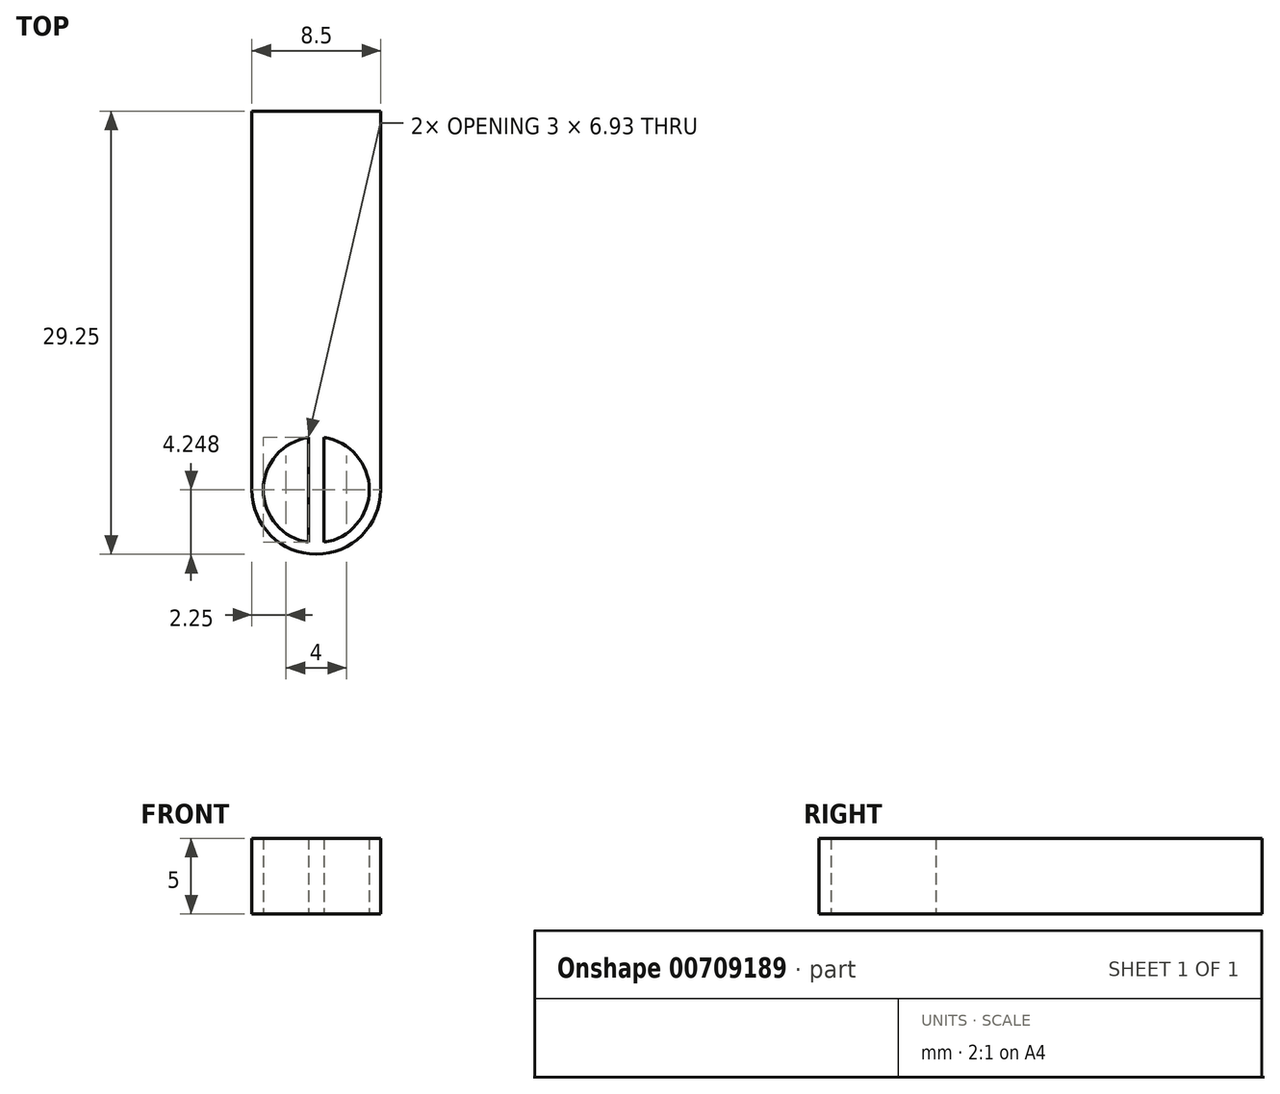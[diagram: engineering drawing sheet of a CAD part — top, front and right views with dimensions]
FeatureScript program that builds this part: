
annotation { "Feature Type Name" : "Feature", "Feature Type Description" : "" }
export const myFeature = defineFeature(function(context is Context, id is Id, definition is map)
    precondition{}
    {
        {
            var Q0;
            Q0=qCreatedBy(makeId("Top.planeOp"),FACE);
            var sketch = newSketch(context, id + "F0", { "sketchPlane" : qUnion([Q0])});
            skArc(sketch, "E0", {"start": v(-4.25, -5.41) * mm, "mid": v(0, -9.66) * mm, "end": v(4.25, -5.41) * mm});
            skLineSegment(sketch, "E1", {"start": v(-4.25, -5.41) * mm, "end": v(-4.25, 19.59) * mm});
            skLineSegment(sketch, "E2", {"start": v(4.25, -5.41) * mm, "end": v(4.25, 19.59) * mm});
            skLineSegment(sketch, "E3", {"start": v(-4.25, 19.59) * mm, "end": v(4.25, 19.59) * mm});
            skLineSegment(sketch, "E4", {"start": v(-0.5, -2.96) * mm, "end": v(-0.5, -7.86) * mm});
            skLineSegment(sketch, "E5.MirrorCS", {"start": v(0.5, -2.96) * mm, "end": v(0.5, -7.86) * mm});
            skArc(sketch, "E6", {"start": v(-0.5, -1.95) * mm, "mid": v(-3.5, -5.41) * mm, "end": v(-0.5, -8.88) * mm});
            skLineSegment(sketch, "E7", {"start": v(-0.5, -7.86) * mm, "end": v(-0.5, -8.88) * mm});
            skLineSegment(sketch, "E8", {"start": v(0.5, -7.86) * mm, "end": v(0.5, -8.88) * mm});
            skLineSegment(sketch, "E9", {"start": v(0.5, -8.88) * mm, "end": v(0.5, -1.95) * mm});
            skLineSegment(sketch, "E10", {"start": v(-0.5, -2.96) * mm, "end": v(-0.5, -1.95) * mm});
            skArc(sketch, "E11.trimOffspring", {"start": v(0.5, -8.88) * mm, "mid": v(3.5, -5.41) * mm, "end": v(0.5, -1.95) * mm});
            skSolve(sketch);
        }
        {
            var Q0;
            Q0=makeQuery(id+"F0.imprint","IMPRINT",FACE,{"disambiguationData":[TD([[makeQuery(id+"F0.imprint","IMPRINT",EDGE,{"derivedFrom":sQuery(id+"F0.wireOp",EDGE,"E0")}),1.0]])]});
            extrude(context, id + "F1", {"entities" : qUnion([Q0]), "depth" : 5 * mm, "offsetDistance" : 25 * mm});
        }
    });
